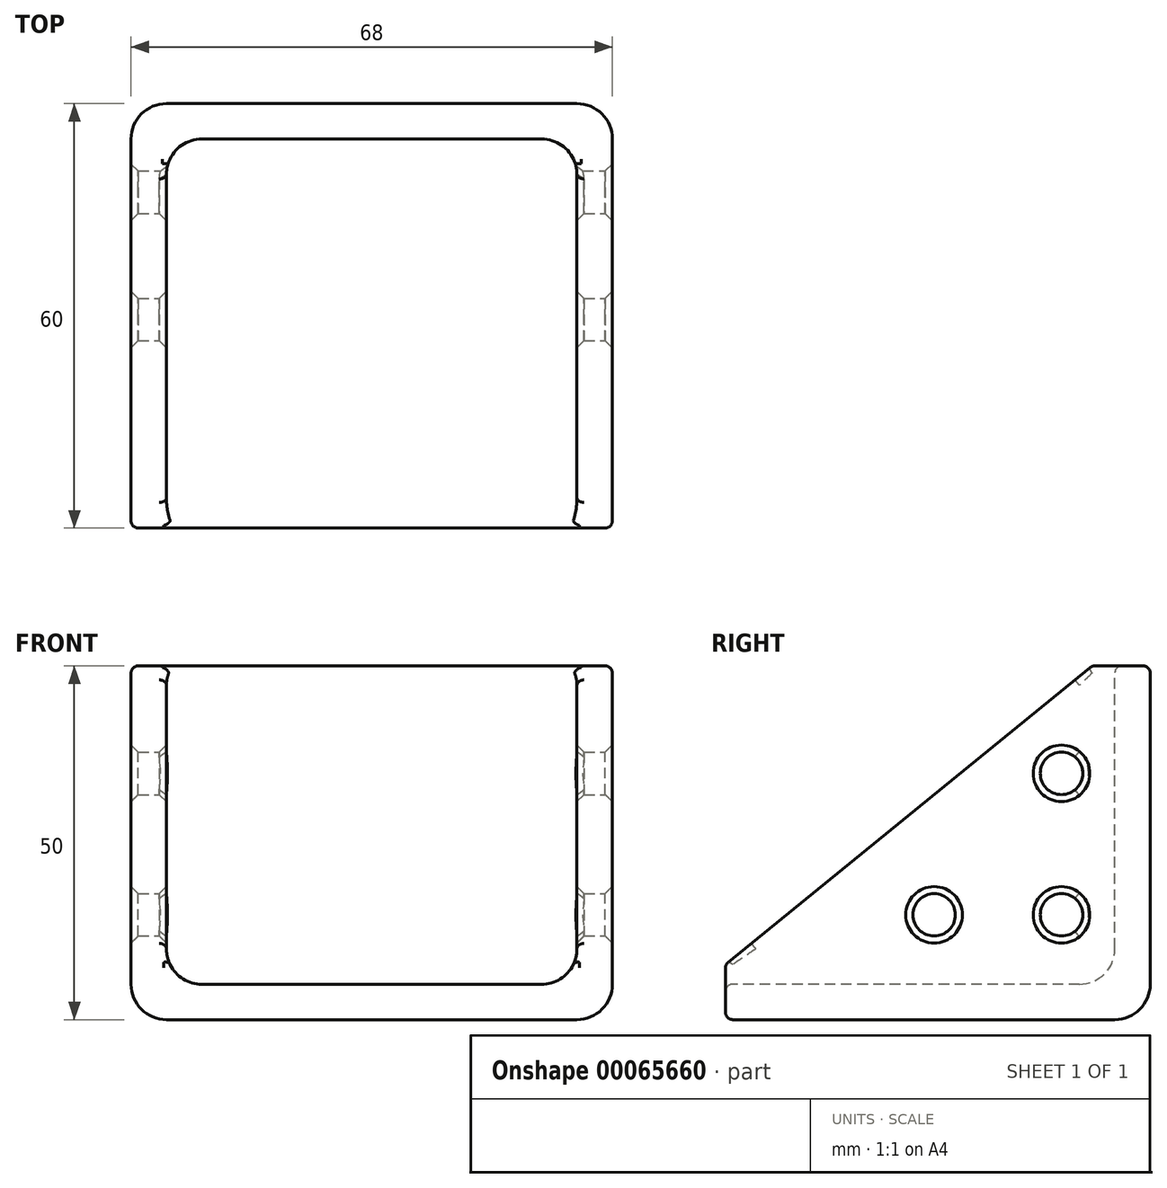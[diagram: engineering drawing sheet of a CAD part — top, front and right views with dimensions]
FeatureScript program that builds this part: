
annotation { "Feature Type Name" : "Feature", "Feature Type Description" : "" }
export const myFeature = defineFeature(function(context is Context, id is Id, definition is map)
    precondition{}
    {
        {
            var Q0;
            Q0=qCreatedBy(makeId("Right.planeOp"),FACE);
            var sketch = newSketch(context, id + "F0", { "sketchPlane" : qUnion([Q0])});
            skLineSegment(sketch, "E0.bottom", {"start": v(32.54, -24.82) * mm, "end": v(-27.46, -24.82) * mm});
            skLineSegment(sketch, "E0.top", {"start": v(32.54, 25.18) * mm, "end": v(24.33, 25.18) * mm});
            skLineSegment(sketch, "E0.left", {"start": v(32.54, -24.82) * mm, "end": v(32.54, 25.18) * mm});
            skLineSegment(sketch, "E0.right", {"start": v(-27.46, -24.82) * mm, "end": v(-27.46, -17) * mm});
            skLineSegment(sketch, "E1", {"start": v(24.33, 25.18) * mm, "end": v(-27.46, -17) * mm});
            skSolve(sketch);
        }
        {
            var Q0;
            Q0=makeQuery(id+"F0.imprint","IMPRINT",FACE,{"disambiguationData":[TD([[makeQuery(id+"F0.imprint","IMPRINT",EDGE,{"derivedFrom":sQuery(id+"F0.wireOp",EDGE,"E0.bottom")}),-1.0]])]});
            extrude(context, id + "F1", {"entities" : qUnion([Q0]), "endBound" : BoundingType.SYMMETRIC, "depth" : 68 * mm});
        }
        {
            var Q0;
            Q0=makeQuery(id+"F1.opExtrude","SWEPT_FACE",FACE,{"disambiguationData":[OSD([sQuery(id+"F0.wireOp",EDGE,"E1")])]});
            var Q1;
            Q1=makeQuery(id+"F1.opExtrude","SWEPT_FACE",FACE,{"disambiguationData":[OSD([sQuery(id+"F0.wireOp",EDGE,"E0.top")])]});
            var Q2;
            Q2=makeQuery(id+"F1.opExtrude","SWEPT_FACE",FACE,{"disambiguationData":[OSD([sQuery(id+"F0.wireOp",EDGE,"E0.right")])]});
            shell(context, id + "F2", {"entities" : qUnion([Q0, Q1, Q2]), "thickness" : 5 * mm});
        }
        {
            var Q0;
            Q0=makeQuery(id+"F1.opExtrude","CAP_EDGE",EDGE,{"disambiguationData":[OSD([sQuery(id+"F0.wireOp",EDGE,"E0.left")])],"isStart":true});
            var Q1;
            Q1=makeQuery(id+"F1.opExtrude","CAP_EDGE",EDGE,{"disambiguationData":[OSD([sQuery(id+"F0.wireOp",EDGE,"E0.left")])],"isStart":false});
            var Q2;
            {var subQ0=sQuery(id+"F0.wireOp",EDGE,"E0.left");Q2=makeQuery(id+"F2.opShell","OFFSET_EDGE",EDGE,{"disambiguationData":[OSD([subQ0]),TDD([makeQuery(id+"F1.opExtrude","CAP_EDGE",EDGE,{"disambiguationData":[OSD([subQ0])],"isStart":false})])]});}
            var Q3;
            {var subQ0=sQuery(id+"F0.wireOp",EDGE,"E0.left");Q3=makeQuery(id+"F2.opShell","OFFSET_EDGE",EDGE,{"disambiguationData":[OSD([subQ0]),TDD([makeQuery(id+"F1.opExtrude","CAP_EDGE",EDGE,{"disambiguationData":[OSD([subQ0])],"isStart":true})])]});}
            var Q4;
            {var subQ0=sQuery(id+"F0.wireOp",EDGE,"E0.bottom");Q4=makeQuery(id+"F2.opShell","OFFSET_EDGE",EDGE,{"disambiguationData":[OSD([subQ0]),TDD([makeQuery(id+"F1.opExtrude","CAP_EDGE",EDGE,{"disambiguationData":[OSD([subQ0])],"isStart":true})])]});}
            var Q5;
            Q5=makeQuery(id+"F2.opShell","OFFSET_EDGE",EDGE,{"disambiguationData":[OSD([sQuery(id+"F0.wireOp",EDGE,"E0.bottom"),sQuery(id+"F0.wireOp",EDGE,"E0.left")])]});
            var Q6;
            {var subQ0=sQuery(id+"F0.wireOp",EDGE,"E0.bottom");Q6=makeQuery(id+"F2.opShell","OFFSET_EDGE",EDGE,{"disambiguationData":[OSD([subQ0]),TDD([makeQuery(id+"F1.opExtrude","CAP_EDGE",EDGE,{"disambiguationData":[OSD([subQ0])],"isStart":false})])]});}
            var Q7;
            Q7=makeQuery(id+"F1.opExtrude","CAP_EDGE",EDGE,{"disambiguationData":[OSD([sQuery(id+"F0.wireOp",EDGE,"E0.bottom")])],"isStart":true});
            var Q8;
            Q8=makeQuery(id+"F1.opExtrude","SWEPT_EDGE",EDGE,{"disambiguationData":[OSD([sQuery(id+"F0.wireOp",EDGE,"E0.bottom"),sQuery(id+"F0.wireOp",EDGE,"E0.left")])]});
            var Q9;
            Q9=makeQuery(id+"F1.opExtrude","CAP_EDGE",EDGE,{"disambiguationData":[OSD([sQuery(id+"F0.wireOp",EDGE,"E0.bottom")])],"isStart":false});
            fillet(context, id + "F3", {"entities" : qUnion([Q0, Q1, Q2, Q3, Q4, Q5, Q6, Q7, Q8, Q9]), "radius" : 5 * mm, "tangentPropagation" : true, "allowEdgeOverflow" : false});
        }
        {
            var Q0;
            {var subQ0=sQuery(id+"F0.wireOp",EDGE,"E1");Q0=makeQuery(id+"F2.opShell","OFFSET_EDGE",EDGE,{"disambiguationData":[OSD([subQ0]),TDD([makeQuery(id+"F1.opExtrude","CAP_EDGE",EDGE,{"disambiguationData":[OSD([subQ0])],"isStart":true})])]});}
            var Q1;
            Q1=makeQuery(id+"F2.opShell","OFFSET_EDGE",EDGE,{"disambiguationData":[OSD([sQuery(id+"F0.wireOp",EDGE,"E0.top"),sQuery(id+"F0.wireOp",EDGE,"E1")])]});
            var Q2;
            Q2=makeQuery(id+"F2.opShell","OFFSET_EDGE",EDGE,{"disambiguationData":[OSD([sQuery(id+"F0.wireOp",EDGE,"E0.right"),sQuery(id+"F0.wireOp",EDGE,"E1")])]});
            var Q3;
            Q3=makeQuery(id+"F1.opExtrude","CAP_EDGE",EDGE,{"disambiguationData":[OSD([sQuery(id+"F0.wireOp",EDGE,"E1")])],"isStart":true});
            var Q4;
            {var subQ0=sQuery(id+"F0.wireOp",EDGE,"E0.bottom");Q4=makeQuery(id+"F3.opFillet","BLEND_EDGE",EDGE,{"blendedFrom":[makeQuery(id+"F2.opShell","OFFSET_EDGE",EDGE,{"disambiguationData":[OSD([subQ0]),TDD([makeQuery(id+"F1.opExtrude","CAP_EDGE",EDGE,{"disambiguationData":[OSD([subQ0])],"isStart":true})])]}),makeQuery(id+"F1.opExtrude","SWEPT_FACE",FACE,{"disambiguationData":[OSD([sQuery(id+"F0.wireOp",EDGE,"E0.right")])]})],"blendedInto":[makeQuery(id+"F1.opExtrude","SWEPT_FACE",FACE,{"disambiguationData":[OSD([sQuery(id+"F0.wireOp",EDGE,"E0.right")])]})]});}
            var Q5;
            Q5=makeQuery(id+"F1.opExtrude","SWEPT_EDGE",EDGE,{"disambiguationData":[OSD([sQuery(id+"F0.wireOp",EDGE,"E0.right"),sQuery(id+"F0.wireOp",EDGE,"E1")])]});
            var Q6;
            Q6=makeQuery(id+"F1.opExtrude","SWEPT_EDGE",EDGE,{"disambiguationData":[OSD([sQuery(id+"F0.wireOp",EDGE,"E0.top"),sQuery(id+"F0.wireOp",EDGE,"E1")])]});
            var Q7;
            {var subQ0=sQuery(id+"F0.wireOp",EDGE,"E1");Q7=makeQuery(id+"F2.opShell","OFFSET_EDGE",EDGE,{"disambiguationData":[OSD([subQ0]),TDD([makeQuery(id+"F1.opExtrude","CAP_EDGE",EDGE,{"disambiguationData":[OSD([subQ0])],"isStart":false})])]});}
            var Q8;
            {var subQ0=sQuery(id+"F0.wireOp",EDGE,"E0.left");Q8=makeQuery(id+"F3.opFillet","BLEND_EDGE",EDGE,{"blendedFrom":[makeQuery(id+"F2.opShell","OFFSET_EDGE",EDGE,{"disambiguationData":[OSD([subQ0]),TDD([makeQuery(id+"F1.opExtrude","CAP_EDGE",EDGE,{"disambiguationData":[OSD([subQ0])],"isStart":false})])]}),makeQuery(id+"F1.opExtrude","SWEPT_FACE",FACE,{"disambiguationData":[OSD([sQuery(id+"F0.wireOp",EDGE,"E0.top")])]})],"blendedInto":[makeQuery(id+"F1.opExtrude","SWEPT_FACE",FACE,{"disambiguationData":[OSD([sQuery(id+"F0.wireOp",EDGE,"E0.top")])]})]});}
            var Q9;
            Q9=makeQuery(id+"F2.opShell","OFFSET_EDGE",EDGE,{"disambiguationData":[OSD([sQuery(id+"F0.wireOp",EDGE,"E0.top"),sQuery(id+"F0.wireOp",EDGE,"E0.left")])]});
            var Q10;
            {var subQ0=sQuery(id+"F0.wireOp",EDGE,"E0.left");Q10=makeQuery(id+"F3.opFillet","BLEND_EDGE",EDGE,{"blendedFrom":[makeQuery(id+"F2.opShell","OFFSET_EDGE",EDGE,{"disambiguationData":[OSD([subQ0]),TDD([makeQuery(id+"F1.opExtrude","CAP_EDGE",EDGE,{"disambiguationData":[OSD([subQ0])],"isStart":true})])]}),makeQuery(id+"F1.opExtrude","SWEPT_FACE",FACE,{"disambiguationData":[OSD([sQuery(id+"F0.wireOp",EDGE,"E0.top")])]})],"blendedInto":[makeQuery(id+"F1.opExtrude","SWEPT_FACE",FACE,{"disambiguationData":[OSD([sQuery(id+"F0.wireOp",EDGE,"E0.top")])]})]});}
            var Q11;
            Q11=makeQuery(id+"F1.opExtrude","CAP_EDGE",EDGE,{"disambiguationData":[OSD([sQuery(id+"F0.wireOp",EDGE,"E0.right")])],"isStart":true});
            var Q12;
            Q12=makeQuery(id+"F1.opExtrude","CAP_EDGE",EDGE,{"disambiguationData":[OSD([sQuery(id+"F0.wireOp",EDGE,"E1")])],"isStart":false});
            var Q13;
            Q13=makeQuery(id+"F1.opExtrude","CAP_EDGE",EDGE,{"disambiguationData":[OSD([sQuery(id+"F0.wireOp",EDGE,"E0.top")])],"isStart":false});
            fillet(context, id + "F4", {"entities" : qUnion([Q0, Q1, Q2, Q3, Q4, Q5, Q6, Q7, Q8, Q9, Q10, Q11, Q12, Q13]), "radius" : 1 * mm, "tangentPropagation" : true, "allowEdgeOverflow" : false});
        }
        {
            var Q0;
            Q0=qCreatedBy(makeId("Right.planeOp"),FACE);
            var sketch = newSketch(context, id + "F5", { "sketchPlane" : qUnion([Q0])});
            skCircle(sketch, "E2", {"center": v(20, -10) * mm, "radius": 3 * mm});
            skCircle(sketch, "E3", {"center": v(20, 10) * mm, "radius": 3 * mm});
            skCircle(sketch, "E4", {"center": v(2, -10) * mm, "radius": 3 * mm});
            skSolve(sketch);
        }
        {
            var Q0;
            Q0=makeQuery(id+"F5.imprint","IMPRINT",FACE,{"disambiguationData":[TD([[makeQuery(id+"F5.imprint","IMPRINT",EDGE,{"derivedFrom":sQuery(id+"F5.wireOp",EDGE,"E3")}),1.0]])]});
            var Q1;
            Q1=makeQuery(id+"F5.imprint","IMPRINT",FACE,{"disambiguationData":[TD([[makeQuery(id+"F5.imprint","IMPRINT",EDGE,{"derivedFrom":sQuery(id+"F5.wireOp",EDGE,"E2")}),1.0]])]});
            var Q2;
            Q2=makeQuery(id+"F5.imprint","IMPRINT",FACE,{"disambiguationData":[TD([[makeQuery(id+"F5.imprint","IMPRINT",EDGE,{"derivedFrom":sQuery(id+"F5.wireOp",EDGE,"E4")}),1.0]])]});
            extrude(context, id + "F6", {"entities" : qUnion([Q0, Q1, Q2]), "operationType" : NewBodyOperationType.REMOVE, "endBound" : BoundingType.SYMMETRIC, "oppositeDirection" : true, "depth" : 100 * mm});
        }
        {
            var Q0;
            Q0=makeQuery(id+"F6.boolean.opBoolean","INTERSECT",EDGE,{"derivedFrom":[makeQuery(id+"F1.opExtrude","CAP_FACE",FACE,{"disambiguationData":[OSD([sQuery(id+"F0.wireOp",EDGE,"E0.bottom"),sQuery(id+"F0.wireOp",EDGE,"E0.top"),sQuery(id+"F0.wireOp",EDGE,"E0.left"),sQuery(id+"F0.wireOp",EDGE,"E0.right"),sQuery(id+"F0.wireOp",EDGE,"E1")])],"isStart":true}),makeQuery(id+"F6.opExtrude","SWEPT_FACE",FACE,{"disambiguationData":[OSD([sQuery(id+"F5.wireOp",EDGE,"E2")])]})]});
            var Q1;
            Q1=makeQuery(id+"F6.boolean.opBoolean","INTERSECT",EDGE,{"derivedFrom":[makeQuery(id+"F1.opExtrude","CAP_FACE",FACE,{"disambiguationData":[OSD([sQuery(id+"F0.wireOp",EDGE,"E0.bottom"),sQuery(id+"F0.wireOp",EDGE,"E0.top"),sQuery(id+"F0.wireOp",EDGE,"E0.left"),sQuery(id+"F0.wireOp",EDGE,"E0.right"),sQuery(id+"F0.wireOp",EDGE,"E1")])],"isStart":true}),makeQuery(id+"F6.opExtrude","SWEPT_FACE",FACE,{"disambiguationData":[OSD([sQuery(id+"F5.wireOp",EDGE,"E3")])]})]});
            var Q2;
            {var subQ0=sQuery(id+"F0.wireOp",EDGE,"E1");var subQ1=sQuery(id+"F0.wireOp",EDGE,"E0.right");var subQ2=sQuery(id+"F0.wireOp",EDGE,"E0.left");var subQ3=sQuery(id+"F0.wireOp",EDGE,"E0.top");var subQ4=sQuery(id+"F0.wireOp",EDGE,"E0.bottom");Q2=makeQuery(id+"F6.boolean.opBoolean","INTERSECT",EDGE,{"derivedFrom":[makeQuery(id+"F2.opShell","OFFSET_FACE",FACE,{"disambiguationData":[OSD([subQ4,subQ3,subQ2,subQ1,subQ0]),TDD([makeQuery(id+"F1.opExtrude","CAP_FACE",FACE,{"disambiguationData":[OSD([subQ4,subQ3,subQ2,subQ1,subQ0])],"isStart":true})])]}),makeQuery(id+"F6.opExtrude","SWEPT_FACE",FACE,{"disambiguationData":[OSD([sQuery(id+"F5.wireOp",EDGE,"E3")])]})]});}
            var Q3;
            {var subQ0=sQuery(id+"F0.wireOp",EDGE,"E1");var subQ1=sQuery(id+"F0.wireOp",EDGE,"E0.right");var subQ2=sQuery(id+"F0.wireOp",EDGE,"E0.left");var subQ3=sQuery(id+"F0.wireOp",EDGE,"E0.top");var subQ4=sQuery(id+"F0.wireOp",EDGE,"E0.bottom");Q3=makeQuery(id+"F6.boolean.opBoolean","INTERSECT",EDGE,{"derivedFrom":[makeQuery(id+"F2.opShell","OFFSET_FACE",FACE,{"disambiguationData":[OSD([subQ4,subQ3,subQ2,subQ1,subQ0]),TDD([makeQuery(id+"F1.opExtrude","CAP_FACE",FACE,{"disambiguationData":[OSD([subQ4,subQ3,subQ2,subQ1,subQ0])],"isStart":true})])]}),makeQuery(id+"F6.opExtrude","SWEPT_FACE",FACE,{"disambiguationData":[OSD([sQuery(id+"F5.wireOp",EDGE,"E2")])]})]});}
            var Q4;
            {var subQ0=sQuery(id+"F0.wireOp",EDGE,"E1");var subQ1=sQuery(id+"F0.wireOp",EDGE,"E0.right");var subQ2=sQuery(id+"F0.wireOp",EDGE,"E0.left");var subQ3=sQuery(id+"F0.wireOp",EDGE,"E0.top");var subQ4=sQuery(id+"F0.wireOp",EDGE,"E0.bottom");Q4=makeQuery(id+"F6.boolean.opBoolean","INTERSECT",EDGE,{"derivedFrom":[makeQuery(id+"F2.opShell","OFFSET_FACE",FACE,{"disambiguationData":[OSD([subQ4,subQ3,subQ2,subQ1,subQ0]),TDD([makeQuery(id+"F1.opExtrude","CAP_FACE",FACE,{"disambiguationData":[OSD([subQ4,subQ3,subQ2,subQ1,subQ0])],"isStart":false})])]}),makeQuery(id+"F6.opExtrude","SWEPT_FACE",FACE,{"disambiguationData":[OSD([sQuery(id+"F5.wireOp",EDGE,"E2")])]})]});}
            var Q5;
            {var subQ0=sQuery(id+"F0.wireOp",EDGE,"E1");var subQ1=sQuery(id+"F0.wireOp",EDGE,"E0.right");var subQ2=sQuery(id+"F0.wireOp",EDGE,"E0.left");var subQ3=sQuery(id+"F0.wireOp",EDGE,"E0.top");var subQ4=sQuery(id+"F0.wireOp",EDGE,"E0.bottom");Q5=makeQuery(id+"F6.boolean.opBoolean","INTERSECT",EDGE,{"derivedFrom":[makeQuery(id+"F2.opShell","OFFSET_FACE",FACE,{"disambiguationData":[OSD([subQ4,subQ3,subQ2,subQ1,subQ0]),TDD([makeQuery(id+"F1.opExtrude","CAP_FACE",FACE,{"disambiguationData":[OSD([subQ4,subQ3,subQ2,subQ1,subQ0])],"isStart":false})])]}),makeQuery(id+"F6.opExtrude","SWEPT_FACE",FACE,{"disambiguationData":[OSD([sQuery(id+"F5.wireOp",EDGE,"E3")])]})]});}
            var Q6;
            Q6=makeQuery(id+"F6.boolean.opBoolean","INTERSECT",EDGE,{"derivedFrom":[makeQuery(id+"F1.opExtrude","CAP_FACE",FACE,{"disambiguationData":[OSD([sQuery(id+"F0.wireOp",EDGE,"E0.bottom"),sQuery(id+"F0.wireOp",EDGE,"E0.top"),sQuery(id+"F0.wireOp",EDGE,"E0.left"),sQuery(id+"F0.wireOp",EDGE,"E0.right"),sQuery(id+"F0.wireOp",EDGE,"E1")])],"isStart":false}),makeQuery(id+"F6.opExtrude","SWEPT_FACE",FACE,{"disambiguationData":[OSD([sQuery(id+"F5.wireOp",EDGE,"E2")])]})]});
            var Q7;
            Q7=makeQuery(id+"F6.boolean.opBoolean","INTERSECT",EDGE,{"derivedFrom":[makeQuery(id+"F1.opExtrude","CAP_FACE",FACE,{"disambiguationData":[OSD([sQuery(id+"F0.wireOp",EDGE,"E0.bottom"),sQuery(id+"F0.wireOp",EDGE,"E0.top"),sQuery(id+"F0.wireOp",EDGE,"E0.left"),sQuery(id+"F0.wireOp",EDGE,"E0.right"),sQuery(id+"F0.wireOp",EDGE,"E1")])],"isStart":false}),makeQuery(id+"F6.opExtrude","SWEPT_FACE",FACE,{"disambiguationData":[OSD([sQuery(id+"F5.wireOp",EDGE,"E3")])]})]});
            var Q8;
            Q8=makeQuery(id+"F6.boolean.opBoolean","INTERSECT",EDGE,{"derivedFrom":[makeQuery(id+"F1.opExtrude","CAP_FACE",FACE,{"disambiguationData":[OSD([sQuery(id+"F0.wireOp",EDGE,"E0.bottom"),sQuery(id+"F0.wireOp",EDGE,"E0.top"),sQuery(id+"F0.wireOp",EDGE,"E0.left"),sQuery(id+"F0.wireOp",EDGE,"E0.right"),sQuery(id+"F0.wireOp",EDGE,"E1")])],"isStart":true}),makeQuery(id+"F6.opExtrude","SWEPT_FACE",FACE,{"disambiguationData":[OSD([sQuery(id+"F5.wireOp",EDGE,"E4")])]})]});
            var Q9;
            {var subQ0=sQuery(id+"F0.wireOp",EDGE,"E1");var subQ1=sQuery(id+"F0.wireOp",EDGE,"E0.right");var subQ2=sQuery(id+"F0.wireOp",EDGE,"E0.left");var subQ3=sQuery(id+"F0.wireOp",EDGE,"E0.top");var subQ4=sQuery(id+"F0.wireOp",EDGE,"E0.bottom");Q9=makeQuery(id+"F6.boolean.opBoolean","INTERSECT",EDGE,{"derivedFrom":[makeQuery(id+"F2.opShell","OFFSET_FACE",FACE,{"disambiguationData":[OSD([subQ4,subQ3,subQ2,subQ1,subQ0]),TDD([makeQuery(id+"F1.opExtrude","CAP_FACE",FACE,{"disambiguationData":[OSD([subQ4,subQ3,subQ2,subQ1,subQ0])],"isStart":true})])]}),makeQuery(id+"F6.opExtrude","SWEPT_FACE",FACE,{"disambiguationData":[OSD([sQuery(id+"F5.wireOp",EDGE,"E4")])]})]});}
            var Q10;
            {var subQ0=sQuery(id+"F0.wireOp",EDGE,"E1");var subQ1=sQuery(id+"F0.wireOp",EDGE,"E0.right");var subQ2=sQuery(id+"F0.wireOp",EDGE,"E0.left");var subQ3=sQuery(id+"F0.wireOp",EDGE,"E0.top");var subQ4=sQuery(id+"F0.wireOp",EDGE,"E0.bottom");Q10=makeQuery(id+"F6.boolean.opBoolean","INTERSECT",EDGE,{"derivedFrom":[makeQuery(id+"F2.opShell","OFFSET_FACE",FACE,{"disambiguationData":[OSD([subQ4,subQ3,subQ2,subQ1,subQ0]),TDD([makeQuery(id+"F1.opExtrude","CAP_FACE",FACE,{"disambiguationData":[OSD([subQ4,subQ3,subQ2,subQ1,subQ0])],"isStart":false})])]}),makeQuery(id+"F6.opExtrude","SWEPT_FACE",FACE,{"disambiguationData":[OSD([sQuery(id+"F5.wireOp",EDGE,"E4")])]})]});}
            var Q11;
            Q11=makeQuery(id+"F6.boolean.opBoolean","INTERSECT",EDGE,{"derivedFrom":[makeQuery(id+"F1.opExtrude","CAP_FACE",FACE,{"disambiguationData":[OSD([sQuery(id+"F0.wireOp",EDGE,"E0.bottom"),sQuery(id+"F0.wireOp",EDGE,"E0.top"),sQuery(id+"F0.wireOp",EDGE,"E0.left"),sQuery(id+"F0.wireOp",EDGE,"E0.right"),sQuery(id+"F0.wireOp",EDGE,"E1")])],"isStart":false}),makeQuery(id+"F6.opExtrude","SWEPT_FACE",FACE,{"disambiguationData":[OSD([sQuery(id+"F5.wireOp",EDGE,"E4")])]})]});
            chamfer(context, id + "F7", {"entities" : qUnion([Q0, Q1, Q2, Q3, Q4, Q5, Q6, Q7, Q8, Q9, Q10, Q11]), "width" : 1 * mm, "tangentPropagation" : true});
        }
    });
